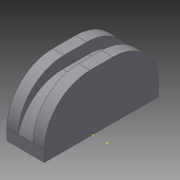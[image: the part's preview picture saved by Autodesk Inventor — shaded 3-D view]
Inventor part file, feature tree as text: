
AUTODESK INVENTOR PART (.ipt)
format: ipt  version: 2015 (Build 190159000, 159)  size: 107,520 bytes
history: native  units: mm
features: sketch x4, extrude x2, fillet x2
ambient origin geometry x8: Origin, YZ Plane, XZ Plane, XY Plane, X Axis, Y Axis, Z Axis, Center Point
bodies: Solid1 (feature_tree)
feature tree (8):
  extrude  "Extrusion1"  Depth=10.0mm TaperAngle=0.0deg
  sketch  "Sketch2"  dims[d4=2.0mm d5=2.0mm d6=2.0mm d7=0.0mm]
  fillet  "Fillet1"  Radius=8.0mm
  sketch  "Sketch3"  dims[d8=8.0mm]
  extrude  "Extrusion2"  Depth=2.0mm
  fillet  "Fillet2"  Radius=2.0mm
  sketch  "Sketch1"  dims[d0=20.0mm d1=10.0mm d2=0.0mm d3=8.0mm]
  sketch  "Sketch4"
